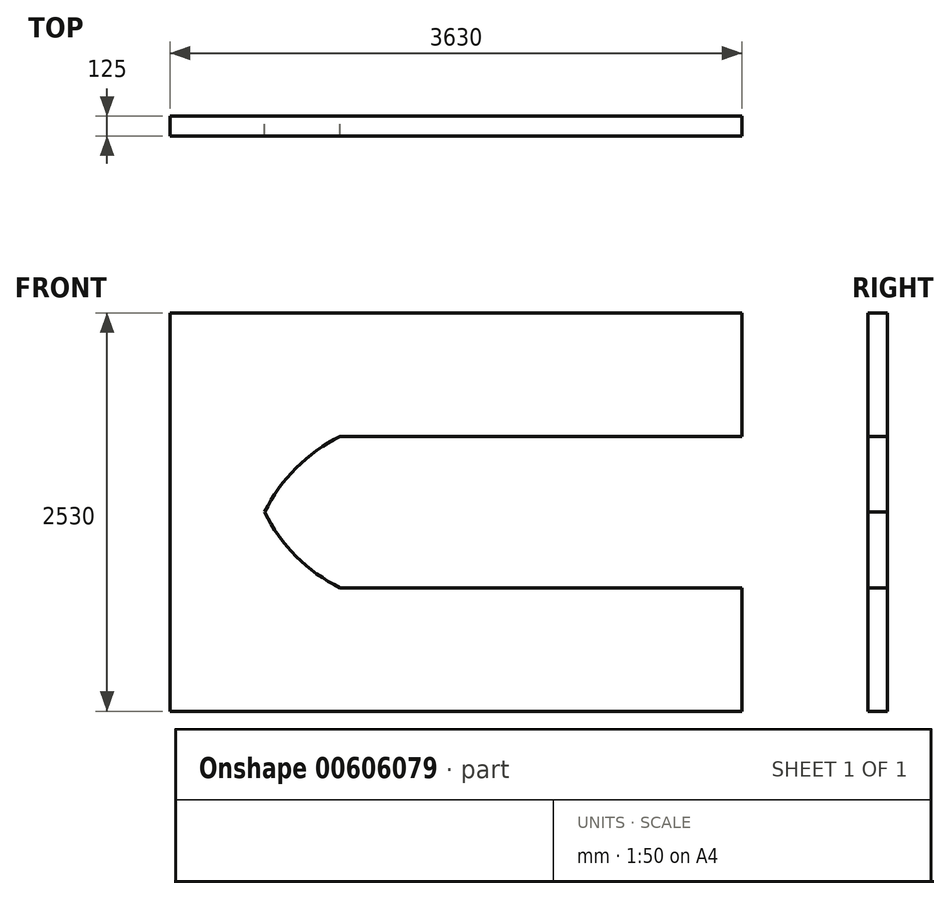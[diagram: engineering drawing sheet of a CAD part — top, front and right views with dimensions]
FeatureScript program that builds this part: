
annotation { "Feature Type Name" : "Feature", "Feature Type Description" : "" }
export const myFeature = defineFeature(function(context is Context, id is Id, definition is map)
    precondition{}
    {
        {
            var Q0;
            Q0=qCreatedBy(makeId("Front.planeOp"),FACE);
            var sketch = newSketch(context, id + "F0", { "sketchPlane" : qUnion([Q0])});
            skLineSegment(sketch, "E0.bottom", {"start": v(-1792.9, 183.5) * mm, "end": v(1837.1, 183.5) * mm});
            skLineSegment(sketch, "E0.top", {"start": v(-1792.9, -1081.5) * mm, "end": v(1837.1, -1081.5) * mm});
            skLineSegment(sketch, "E0.left", {"start": v(-1792.9, 183.5) * mm, "end": v(-1792.9, -1081.5) * mm});
            skLineSegment(sketch, "E0.right", {"start": v(1837.1, 183.5) * mm, "end": v(1837.1, -1081.5) * mm});
            skSolve(sketch);
        }
        {
            var Q0;
            Q0=makeQuery(id+"F0.imprint","IMPRINT",FACE,{"disambiguationData":[TD([[makeQuery(id+"F0.imprint","IMPRINT",EDGE,{"derivedFrom":sQuery(id+"F0.wireOp",EDGE,"E0.bottom")}),-1.0]])]});
            extrude(context, id + "F1", {"entities" : qUnion([Q0]), "depth" : 125 * mm, "offsetDistance" : 25 * mm});
        }
        {
            var Q0;
            Q0=makeQuery(id+"F1.opExtrude","CAP_FACE",FACE,{"disambiguationData":[OSD([sQuery(id+"F0.wireOp",EDGE,"E0.bottom"),sQuery(id+"F0.wireOp",EDGE,"E0.top"),sQuery(id+"F0.wireOp",EDGE,"E0.left"),sQuery(id+"F0.wireOp",EDGE,"E0.right")])],"isStart":true});
            var sketch = newSketch(context, id + "F2", { "sketchPlane" : qUnion([Q0])});
            skLineSegment(sketch, "E1", {"start": v(-1237.1, 183.5) * mm, "end": v(-757.1, -296.5) * mm});
            skLineSegment(sketch, "E2", {"start": v(712.9, -296.5) * mm, "end": v(1192.9, 183.5) * mm});
            skLineSegment(sketch, "E3", {"start": v(-757.1, -296.5) * mm, "end": v(712.9, -296.5) * mm});
            skLineSegment(sketch, "E4", {"start": v(-1237.1, 183.5) * mm, "end": v(1192.9, 183.5) * mm});
            skSolve(sketch);
        }
        {
            var Q0;
            Q0 = qSketchRegion(id + "F2", true);
            extrude(context, id + "F3", {"entities" : qUnion([Q0]), "operationType" : NewBodyOperationType.REMOVE, "endBound" : BoundingType.UP_TO_NEXT, "oppositeDirection" : true, "depth" : 125 * mm, "offsetDistance" : 25 * mm});
        }
        {
            var Q0;
            Q0=makeQuery(id+"F1.opExtrude","CAP_FACE",FACE,{"disambiguationData":[OSD([sQuery(id+"F0.wireOp",EDGE,"E0.bottom"),sQuery(id+"F0.wireOp",EDGE,"E0.top"),sQuery(id+"F0.wireOp",EDGE,"E0.left"),sQuery(id+"F0.wireOp",EDGE,"E0.right")])],"isStart":false});
            var sketch = newSketch(context, id + "F4", { "sketchPlane" : qUnion([Q0])});
            skLineSegment(sketch, "E5", {"start": v(757.1, -296.5) * mm, "end": v(1237.1, 183.5) * mm});
            skLineSegment(sketch, "E6", {"start": v(1237.1, 183.5) * mm, "end": v(1837.1, 183.5) * mm});
            skLineSegment(sketch, "E7", {"start": v(1837.1, 183.5) * mm, "end": v(1837.1, -296.5) * mm});
            skLineSegment(sketch, "E8", {"start": v(1837.1, -296.5) * mm, "end": v(757.1, -296.5) * mm});
            skSolve(sketch);
        }
        {
            var Q0;
            Q0=makeQuery(id+"F4.imprint","IMPRINT",FACE,{"disambiguationData":[TD([[makeQuery(id+"F4.imprint","IMPRINT",EDGE,{"derivedFrom":sQuery(id+"F4.wireOp",EDGE,"E5")}),1.0]])]});
            extrude(context, id + "F5", {"entities" : qUnion([Q0]), "operationType" : NewBodyOperationType.REMOVE, "endBound" : BoundingType.UP_TO_NEXT, "oppositeDirection" : true, "depth" : 25 * mm, "offsetDistance" : 25 * mm});
        }
        {
            var Q0;
            Q0=makeQuery(id+"F1.opExtrude","CAP_FACE",FACE,{"disambiguationData":[OSD([sQuery(id+"F0.wireOp",EDGE,"E0.bottom"),sQuery(id+"F0.wireOp",EDGE,"E0.top"),sQuery(id+"F0.wireOp",EDGE,"E0.left"),sQuery(id+"F0.wireOp",EDGE,"E0.right")])],"isStart":false});
            var sketch = newSketch(context, id + "F6", { "sketchPlane" : qUnion([Q0])});
            skArc(sketch, "E9", {"start": v(-1192.9, 183.5) * mm, "mid": v(-993.47, -97.08) * mm, "end": v(-712.9, -296.5) * mm});
            skLineSegment(sketch, "E10", {"start": v(-1192.9, 183.5) * mm, "end": v(-712.9, -296.5) * mm});
            skSolve(sketch);
        }
        {
            var Q0;
            Q0=makeQuery(id+"F6.imprint","IMPRINT",FACE,{"disambiguationData":[TD([[makeQuery(id+"F6.imprint","IMPRINT",EDGE,{"derivedFrom":sQuery(id+"F6.wireOp",EDGE,"E9")}),1.0]])]});
            extrude(context, id + "F7", {"entities" : qUnion([Q0]), "operationType" : NewBodyOperationType.REMOVE, "endBound" : BoundingType.UP_TO_NEXT, "oppositeDirection" : true, "depth" : 25 * mm, "offsetDistance" : 25 * mm});
        }
        {
            var Q0;
            Q0=makeQuery(id+"F1.opExtrude","SWEPT_BODY",BODY,{"disambiguationData":[OSD([sQuery(id+"F0.wireOp",EDGE,"E0.bottom"),sQuery(id+"F0.wireOp",EDGE,"E0.top"),sQuery(id+"F0.wireOp",EDGE,"E0.left"),sQuery(id+"F0.wireOp",EDGE,"E0.right")])]});
            var Q1;
            {var subQ1=sQuery(id+"F0.wireOp",EDGE,"E0.left");var subQ3=sQuery(id+"F0.wireOp",EDGE,"E0.bottom");Q1=makeQuery(id+"F3.boolean.opBoolean","SPLIT",FACE,{"disambiguationData":[TD([makeQuery(id+"F1.opExtrude","SWEPT_FACE",FACE,{"disambiguationData":[OSD([subQ1])]})])],"derivedFrom":makeQuery(id+"F1.opExtrude","SWEPT_FACE",FACE,{"disambiguationData":[OSD([subQ3])]})});}
            mirror(context, id + "F8", {"operationType" : NewBodyOperationType.ADD, "entities" : qUnion([Q0]), "mirrorPlane" : qUnion([Q1])});
        }
    });
